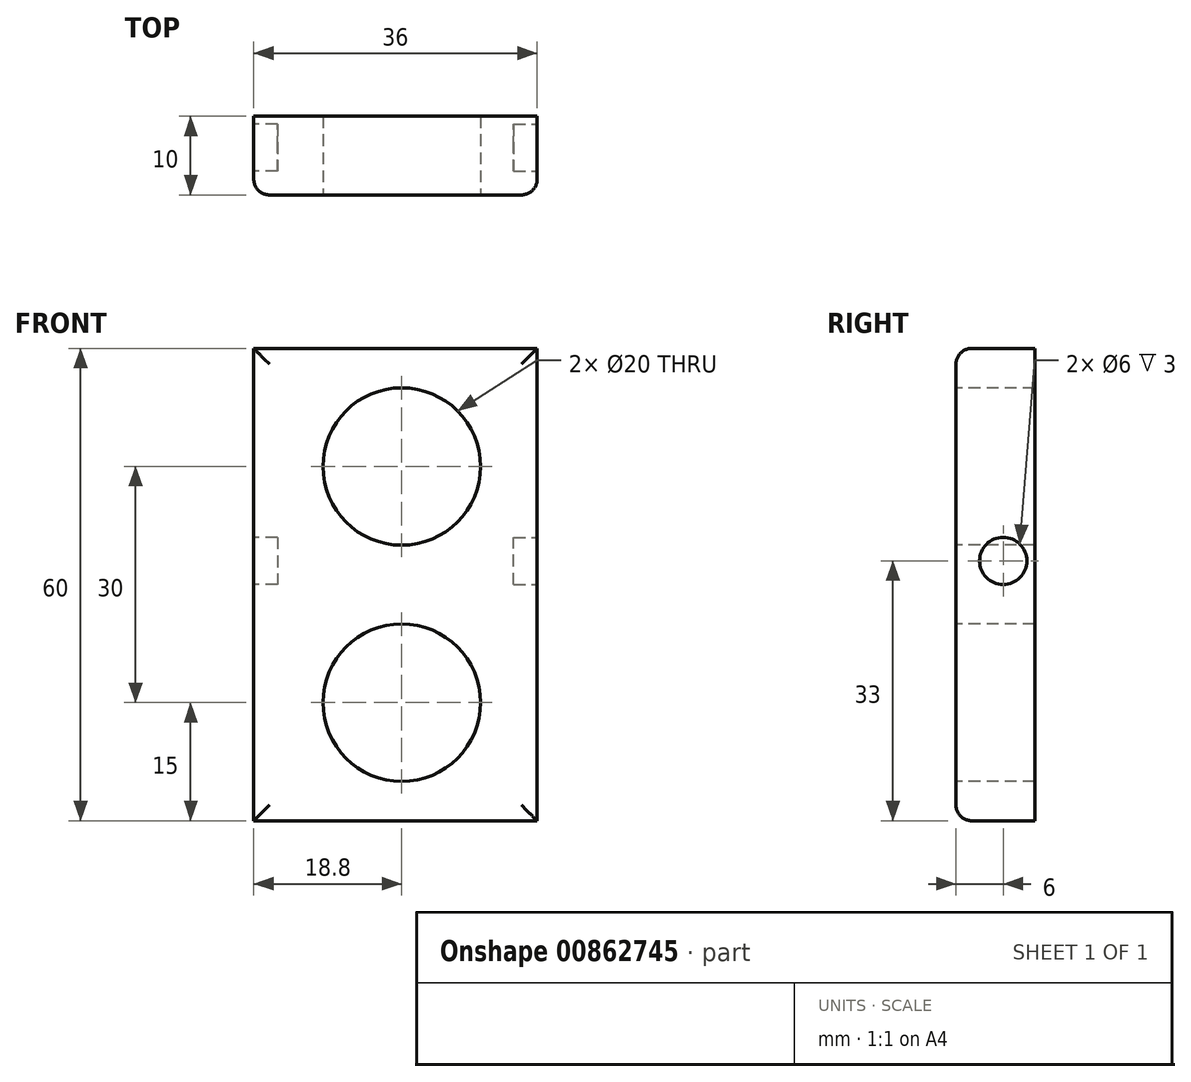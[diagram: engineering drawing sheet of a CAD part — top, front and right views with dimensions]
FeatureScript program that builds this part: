
annotation { "Feature Type Name" : "Feature", "Feature Type Description" : "" }
export const myFeature = defineFeature(function(context is Context, id is Id, definition is map)
    precondition{}
    {
        {
            var Q0;
            Q0=qCreatedBy(makeId("Front.planeOp"),FACE);
            var sketch = newSketch(context, id + "F0", { "sketchPlane" : qUnion([Q0])});
            skLineSegment(sketch, "E0", {"start": v(0, 0) * mm, "end": v(0, 60) * mm});
            skLineSegment(sketch, "E1", {"start": v(0, 60) * mm, "end": v(36, 60) * mm});
            skLineSegment(sketch, "E2", {"start": v(36, 60) * mm, "end": v(36, 0) * mm});
            skLineSegment(sketch, "E3", {"start": v(36, 0) * mm, "end": v(0, 0) * mm});
            skSolve(sketch);
        }
        {
            var Q0;
            Q0=makeQuery(id+"F0.imprint","IMPRINT",FACE,{"disambiguationData":[TD([[makeQuery(id+"F0.imprint","IMPRINT",EDGE,{"derivedFrom":sQuery(id+"F0.wireOp",EDGE,"E0")}),-1.0]])]});
            extrude(context, id + "F1", {"entities" : qUnion([Q0]), "depth" : 10 * mm, "offsetDistance" : 25 * mm});
        }
        {
            var Q0;
            Q0=makeQuery(id+"F1.opExtrude","CAP_FACE",FACE,{"disambiguationData":[OSD([sQuery(id+"F0.wireOp",EDGE,"E0"),sQuery(id+"F0.wireOp",EDGE,"E1"),sQuery(id+"F0.wireOp",EDGE,"E2"),sQuery(id+"F0.wireOp",EDGE,"E3")])],"isStart":false});
            fillet(context, id + "F2", {"entities" : qUnion([Q0]), "radius" : 2 * mm, "tangentPropagation" : true, "allowEdgeOverflow" : false});
        }
        {
            var Q0;
            Q0=makeQuery(id+"F1.opExtrude","CAP_FACE",FACE,{"disambiguationData":[OSD([sQuery(id+"F0.wireOp",EDGE,"E0"),sQuery(id+"F0.wireOp",EDGE,"E1"),sQuery(id+"F0.wireOp",EDGE,"E2"),sQuery(id+"F0.wireOp",EDGE,"E3")])],"isStart":false});
            var sketch = newSketch(context, id + "F3", { "sketchPlane" : qUnion([Q0])});
            skCircle(sketch, "E4", {"center": v(18.8, 45) * mm, "radius": 10 * mm});
            skCircle(sketch, "E5", {"center": v(18.8, 15) * mm, "radius": 10 * mm});
            skSolve(sketch);
        }
        {
            var Q0;
            Q0=makeQuery(id+"F3.imprint","IMPRINT",FACE,{"disambiguationData":[TD([[makeQuery(id+"F3.imprint","IMPRINT",EDGE,{"derivedFrom":sQuery(id+"F3.wireOp",EDGE,"E5")}),1.0]])]});
            var Q1;
            Q1=makeQuery(id+"F3.imprint","IMPRINT",FACE,{"disambiguationData":[TD([[makeQuery(id+"F3.imprint","IMPRINT",EDGE,{"derivedFrom":sQuery(id+"F3.wireOp",EDGE,"E4")}),1.0]])]});
            extrude(context, id + "F4", {"entities" : qUnion([Q0, Q1]), "operationType" : NewBodyOperationType.REMOVE, "oppositeDirection" : true, "depth" : 25 * mm, "offsetDistance" : 25 * mm});
        }
        {
            var Q0;
            Q0=makeQuery(id+"F1.opExtrude","SWEPT_FACE",FACE,{"disambiguationData":[OSD([sQuery(id+"F0.wireOp",EDGE,"E2")])]});
            var sketch = newSketch(context, id + "F5", { "sketchPlane" : qUnion([Q0])});
            skCircle(sketch, "E6", {"center": v(-4, 33) * mm, "radius": 3 * mm});
            skSolve(sketch);
        }
        {
            var Q0;
            Q0=makeQuery(id+"F5.imprint","IMPRINT",FACE,{"disambiguationData":[TD([[makeQuery(id+"F5.imprint","IMPRINT",EDGE,{"derivedFrom":sQuery(id+"F5.wireOp",EDGE,"E6")}),1.0]])]});
            extrude(context, id + "F6", {"entities" : qUnion([Q0]), "operationType" : NewBodyOperationType.REMOVE, "oppositeDirection" : true, "depth" : 3 * mm, "offsetDistance" : 25 * mm});
        }
        {
            var Q0;
            Q0=makeQuery(id+"F1.opExtrude","SWEPT_FACE",FACE,{"disambiguationData":[OSD([sQuery(id+"F0.wireOp",EDGE,"E0")])]});
            var sketch = newSketch(context, id + "F7", { "sketchPlane" : qUnion([Q0])});
            skCircle(sketch, "E7", {"center": v(4, 33) * mm, "radius": 3 * mm});
            skSolve(sketch);
        }
        {
            var Q0;
            Q0=makeQuery(id+"F7.imprint","IMPRINT",FACE,{"disambiguationData":[TD([[makeQuery(id+"F7.imprint","IMPRINT",EDGE,{"derivedFrom":sQuery(id+"F7.wireOp",EDGE,"E7")}),1.0]])]});
            var Q1;
            Q1=sQuery(id+"F7.wireOp",EDGE,"E7");
            extrude(context, id + "F8", {"entities" : qUnion([Q0]), "operationType" : NewBodyOperationType.REMOVE, "surfaceEntities" : qUnion([Q1]), "oppositeDirection" : true, "depth" : 3 * mm, "offsetDistance" : 25 * mm});
        }
    });
